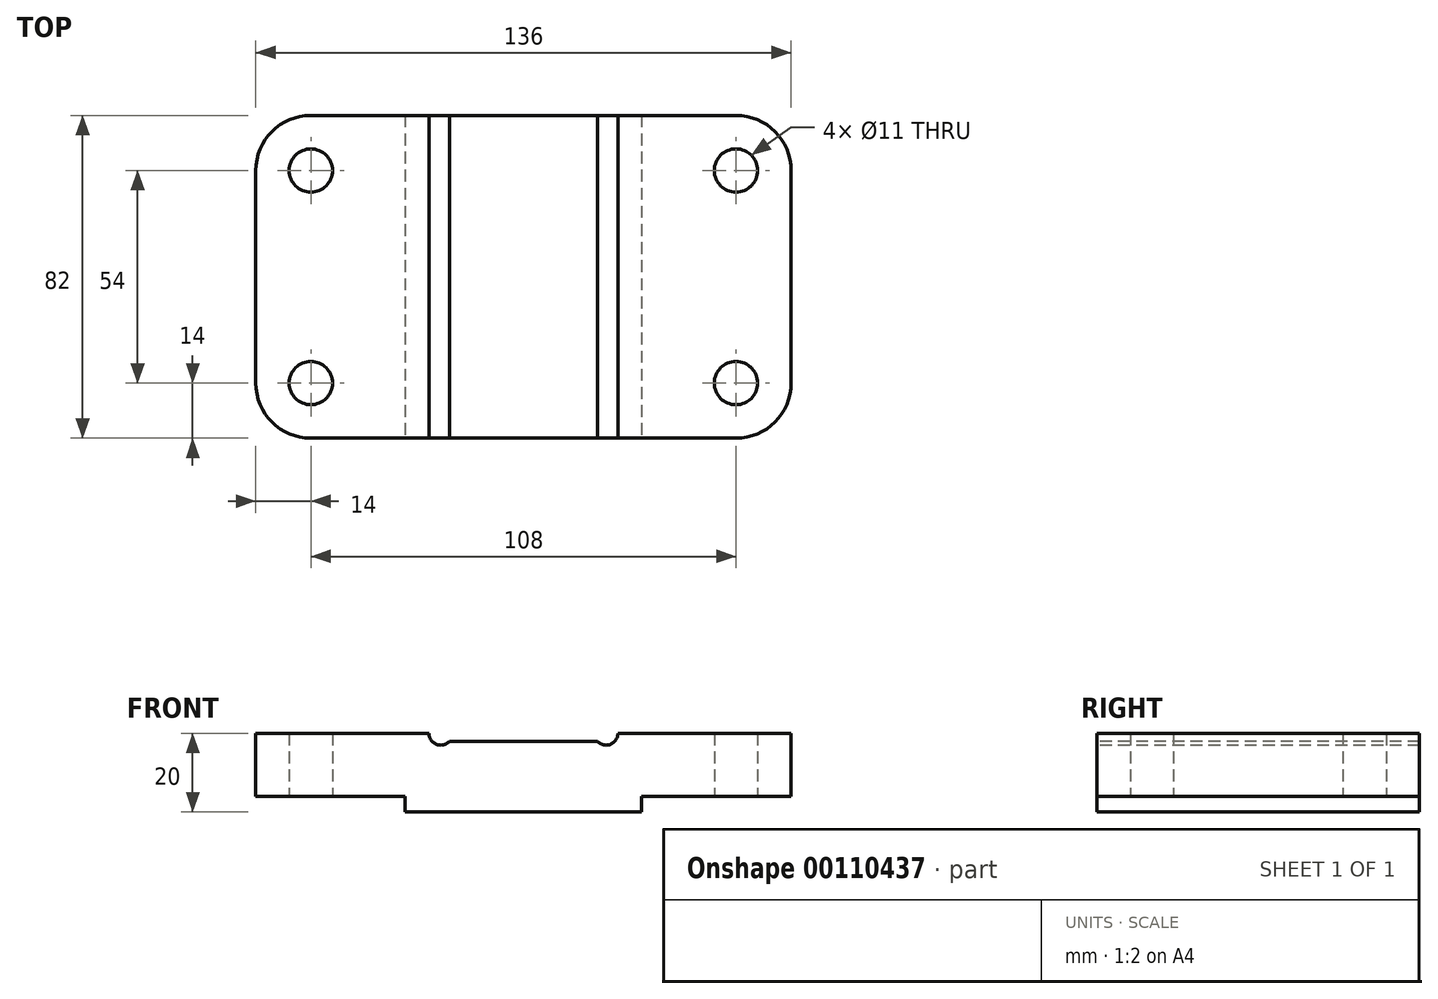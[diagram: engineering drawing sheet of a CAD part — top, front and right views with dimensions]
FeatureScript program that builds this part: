
annotation { "Feature Type Name" : "Feature", "Feature Type Description" : "" }
export const myFeature = defineFeature(function(context is Context, id is Id, definition is map)
    precondition{}
    {
        {
            var Q0;
            Q0=qCreatedBy(makeId("Front.planeOp"),FACE);
            var sketch = newSketch(context, id + "F0", { "sketchPlane" : qUnion([Q0])});
            skLineSegment(sketch, "E0", {"start": v(0, 0) * mm, "end": v(0, 16) * mm});
            skLineSegment(sketch, "E1", {"start": v(0, 16) * mm, "end": v(44, 16) * mm});
            skArc(sketch, "E2", {"start": v(44, 16) * mm, "mid": v(45.93, 13.2) * mm, "end": v(49.24, 14) * mm});
            skLineSegment(sketch, "E3", {"start": v(49.24, 14) * mm, "end": v(86.76, 14) * mm});
            skArc(sketch, "E4", {"start": v(86.76, 14) * mm, "mid": v(90.07, 13.2) * mm, "end": v(92, 16) * mm});
            skLineSegment(sketch, "E5", {"start": v(92, 16) * mm, "end": v(136, 16) * mm});
            skLineSegment(sketch, "E6", {"start": v(136, 16) * mm, "end": v(136, 0) * mm});
            skLineSegment(sketch, "E7", {"start": v(136, 0) * mm, "end": v(98, 0) * mm});
            skLineSegment(sketch, "E8", {"start": v(98, 0) * mm, "end": v(98, -4) * mm});
            skLineSegment(sketch, "E9", {"start": v(98, -4) * mm, "end": v(38, -4) * mm});
            skLineSegment(sketch, "E10", {"start": v(38, -4) * mm, "end": v(38, 0) * mm});
            skLineSegment(sketch, "E11", {"start": v(38, 0) * mm, "end": v(0, 0) * mm});
            skLineSegment(sketch, "E12", {"start": v(44, 16) * mm, "end": v(136, 16) * mm, "construction": true});
            skSolve(sketch);
        }
        {
            var Q0;
            Q0=makeQuery(id+"F0.imprint","IMPRINT",FACE,{"disambiguationData":[TD([[makeQuery(id+"F0.imprint","IMPRINT",EDGE,{"derivedFrom":sQuery(id+"F0.wireOp",EDGE,"E0")}),-1.0]])]});
            extrude(context, id + "F1", {"entities" : qUnion([Q0]), "oppositeDirection" : true, "depth" : 82 * mm});
        }
        {
            var Q0;
            Q0=qCreatedBy(makeId("Top.planeOp"),FACE);
            var sketch = newSketch(context, id + "F2", { "sketchPlane" : qUnion([Q0])});
            skCircle(sketch, "E13", {"center": v(14, 68) * mm, "radius": 5.5 * mm});
            skLineSegment(sketch, "E14", {"start": v(0, 0) * mm, "end": v(0, 82) * mm, "construction": true});
            skLineSegment(sketch, "E15", {"start": v(0, 41) * mm, "end": v(139.95, 41) * mm, "construction": true});
            skPoint(sketch, "E15.endSnap0", {"position": v(0, 41) * mm});
            skCircle(sketch, "E16.MirrorC", {"center": v(14, 14) * mm, "radius": 5.5 * mm});
            skLineSegment(sketch, "E17", {"start": v(49.24, 82) * mm, "end": v(86.76, 82) * mm, "construction": true});
            skLineSegment(sketch, "E18", {"start": v(68, 82) * mm, "end": v(68, 0) * mm, "construction": true});
            skLineSegment(sketch, "E19.MirrorCS", {"start": v(136, 41) * mm, "end": v(-3.95, 41) * mm, "construction": true});
            skLineSegment(sketch, "E20.MirrorCS", {"start": v(86.76, 82) * mm, "end": v(49.24, 82) * mm, "construction": true});
            skCircle(sketch, "E21.MirrorC", {"center": v(122, 68) * mm, "radius": 5.5 * mm});
            skCircle(sketch, "E22.MirrorC", {"center": v(122, 14) * mm, "radius": 5.5 * mm});
            skSolve(sketch);
        }
        {
            var Q0;
            Q0 = qSketchRegion(id + "F2", true);
            var Q1;
            Q1=sQuery(id+"F2.wireOp",EDGE,"E13");
            var Q2;
            Q2=sQuery(id+"F2.wireOp",EDGE,"E21.MirrorC");
            var Q3;
            Q3=sQuery(id+"F2.wireOp",EDGE,"E22.MirrorC");
            var Q4;
            Q4=sQuery(id+"F2.wireOp",EDGE,"E16.MirrorC");
            extrude(context, id + "F3", {"entities" : qUnion([Q0]), "operationType" : NewBodyOperationType.REMOVE, "surfaceEntities" : qUnion([Q1, Q2, Q3, Q4]), "endBound" : BoundingType.THROUGH_ALL, "depth" : 25 * mm});
        }
        {
            var Q0;
            Q0=makeQuery(id+"F1.opExtrude","CAP_EDGE",EDGE,{"disambiguationData":[OSD([sQuery(id+"F0.wireOp",EDGE,"E6")])],"isStart":true});
            var Q1;
            Q1=makeQuery(id+"F1.opExtrude","CAP_EDGE",EDGE,{"disambiguationData":[OSD([sQuery(id+"F0.wireOp",EDGE,"E6")])],"isStart":false});
            fillet(context, id + "F4", {"entities" : qUnion([Q0, Q1]), "radius" : 14 * mm, "tangentPropagation" : true, "allowEdgeOverflow" : false});
        }
        {
            var Q0;
            Q0=makeQuery(id+"F1.opExtrude","CAP_EDGE",EDGE,{"disambiguationData":[OSD([sQuery(id+"F0.wireOp",EDGE,"E0")])],"isStart":true});
            var Q1;
            Q1=makeQuery(id+"F1.opExtrude","CAP_EDGE",EDGE,{"disambiguationData":[OSD([sQuery(id+"F0.wireOp",EDGE,"E0")])],"isStart":false});
            fillet(context, id + "F5", {"entities" : qUnion([Q0, Q1]), "radius" : 14 * mm, "tangentPropagation" : true, "allowEdgeOverflow" : false});
        }
    });
